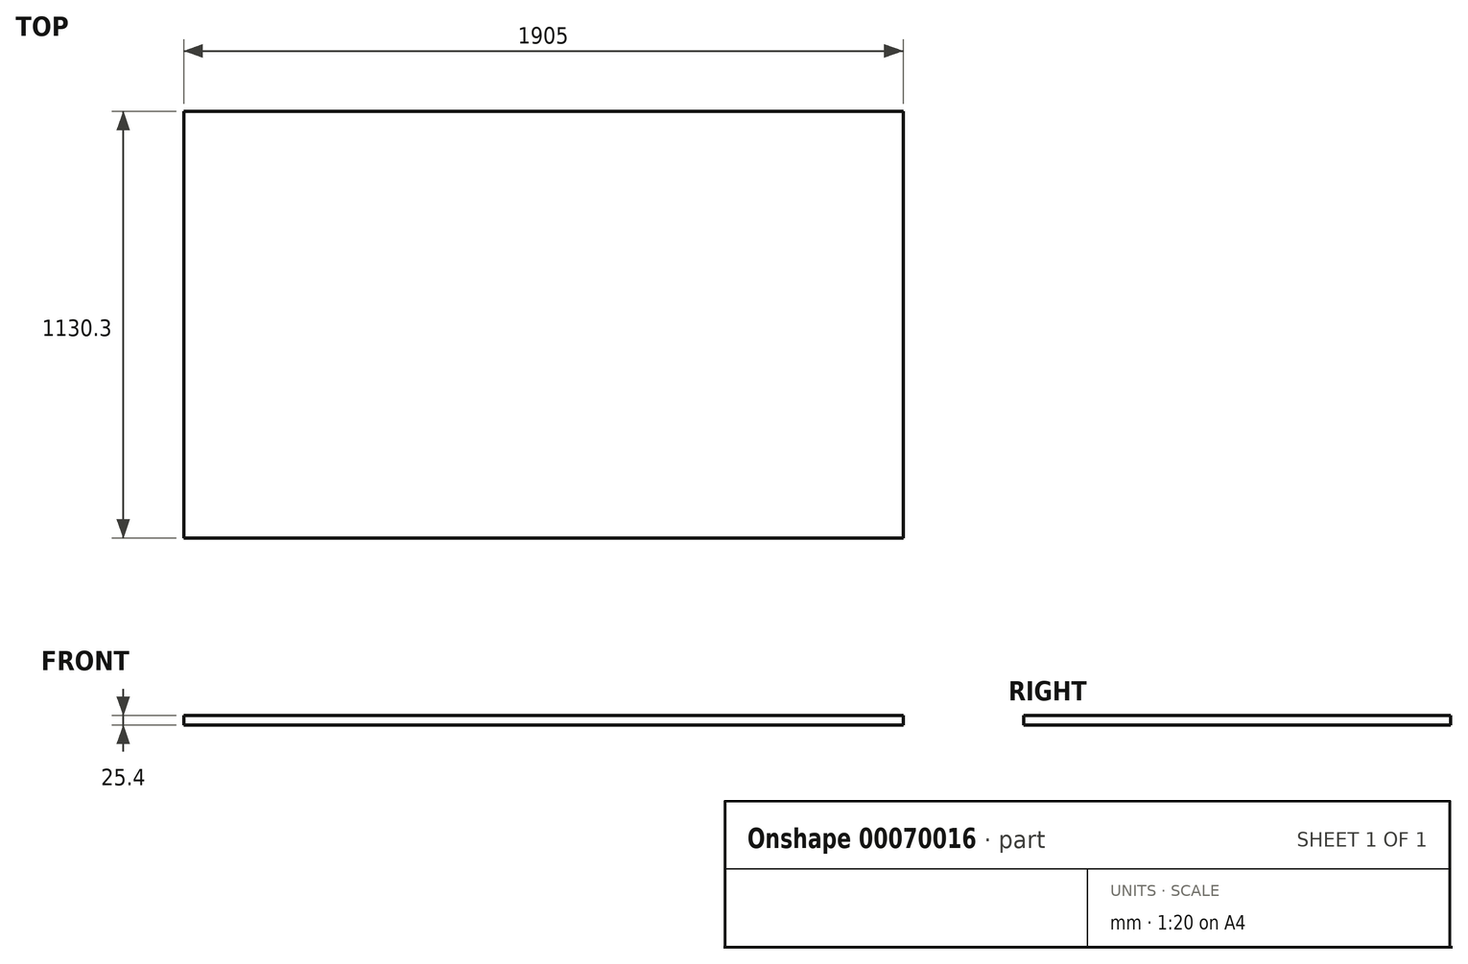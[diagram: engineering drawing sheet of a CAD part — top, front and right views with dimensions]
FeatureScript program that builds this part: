
annotation { "Feature Type Name" : "Feature", "Feature Type Description" : "" }
export const myFeature = defineFeature(function(context is Context, id is Id, definition is map)
    precondition{}
    {
        {
            var Q0;
            Q0=qCreatedBy(makeId("Top.planeOp"),FACE);
            var sketch = newSketch(context, id + "F0", { "sketchPlane" : qUnion([Q0])});
            skLineSegment(sketch, "E0.bottom", {"start": v(0, 0) * mm, "end": v(1905, 0) * mm});
            skLineSegment(sketch, "E0.top", {"start": v(0, 1130.3) * mm, "end": v(1905, 1130.3) * mm});
            skLineSegment(sketch, "E0.left", {"start": v(0, 0) * mm, "end": v(0, 1130.3) * mm});
            skLineSegment(sketch, "E0.right", {"start": v(1905, 0) * mm, "end": v(1905, 1130.3) * mm});
            skSolve(sketch);
        }
        {
            var Q0;
            Q0=makeQuery(id+"F0.imprint","IMPRINT",FACE,{"disambiguationData":[TD([[makeQuery(id+"F0.imprint","IMPRINT",EDGE,{"derivedFrom":sQuery(id+"F0.wireOp",EDGE,"E0.bottom")}),1.0]])]});
            extrude(context, id + "F1", {"entities" : qUnion([Q0]), "depth" : 25.4 * mm});
        }
    });
